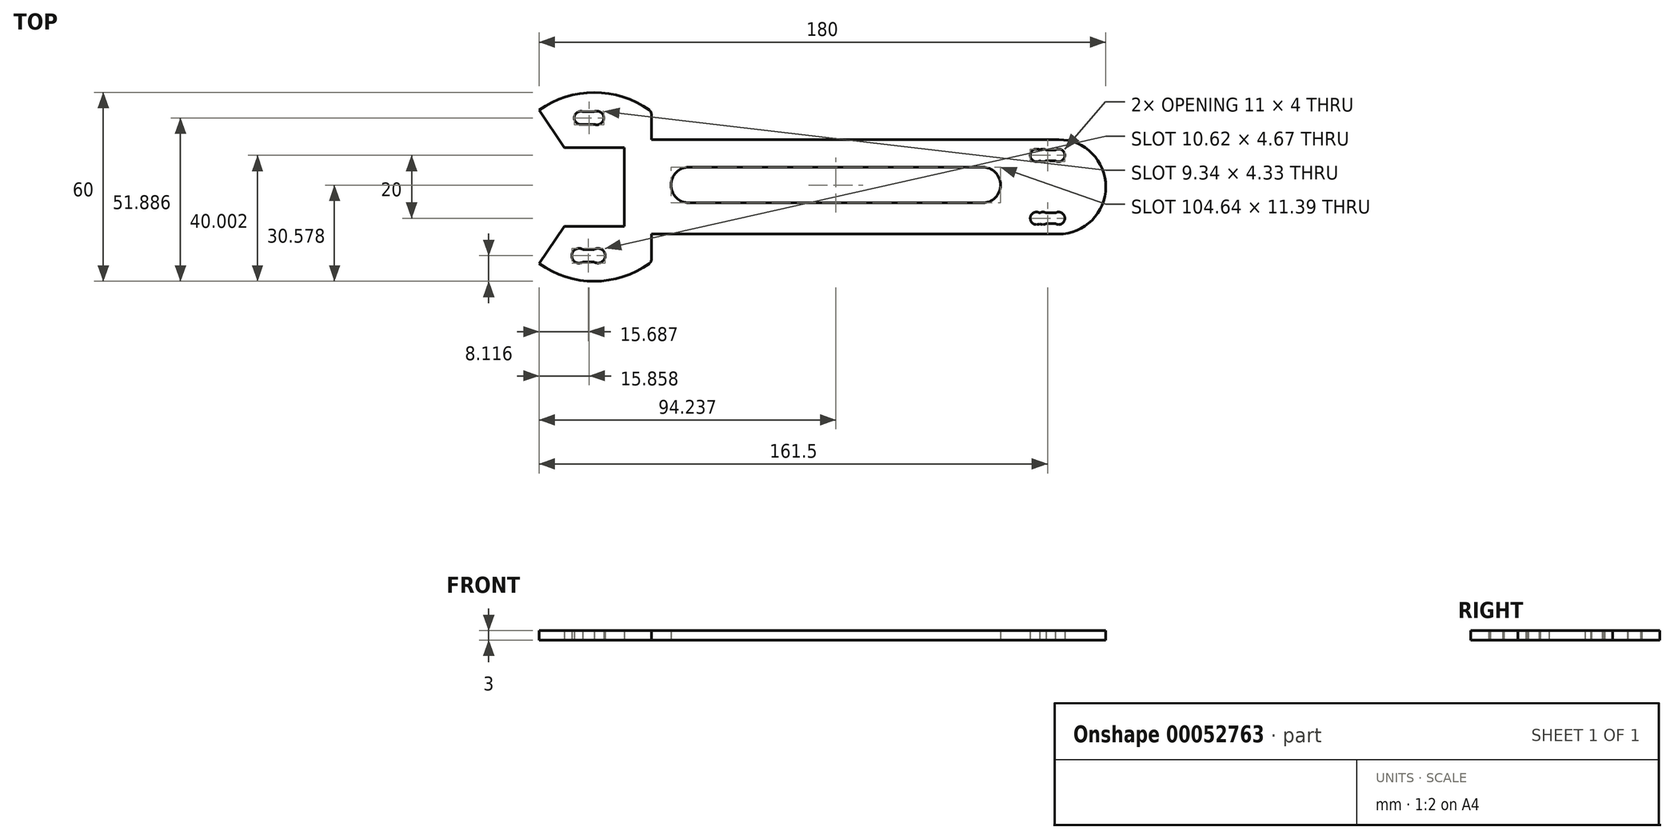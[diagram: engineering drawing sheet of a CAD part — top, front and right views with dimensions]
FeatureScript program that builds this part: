
annotation { "Feature Type Name" : "Feature", "Feature Type Description" : "" }
export const myFeature = defineFeature(function(context is Context, id is Id, definition is map)
    precondition{}
    {
        {
            var Q0;
            Q0=qCreatedBy(makeId("Top.planeOp"),FACE);
            var sketch = newSketch(context, id + "F0", { "sketchPlane" : qUnion([Q0])});
            skLineSegment(sketch, "E0.left", {"start": v(-8.16, -5.77) * mm, "end": v(-8.16, 19.23) * mm});
            skLineSegment(sketch, "E0.right", {"start": v(10.84, -5.77) * mm, "end": v(10.84, 19.23) * mm});
            skArc(sketch, "E1", {"start": v(-16.16, -17.64) * mm, "mid": v(1.75, -23.27) * mm, "end": v(19.5, -17.15) * mm});
            skPoint(sketch, "E2", {"position": v(10.84, 6.73) * mm});
            skLineSegment(sketch, "E3", {"start": v(10.84, 15.23) * mm, "end": v(-8.16, 19.23) * mm});
            skLineSegment(sketch, "E4", {"start": v(10.84, -1.77) * mm, "end": v(8.22, -2.32) * mm});
            skLineSegment(sketch, "E5", {"start": v(10.84, 15.23) * mm, "end": v(10.84, -1.77) * mm});
            skLineSegment(sketch, "E6", {"start": v(-8.16, -5.77) * mm, "end": v(10.84, -5.77) * mm});
            skLineSegment(sketch, "E7", {"start": v(10.84, 19.23) * mm, "end": v(-8.16, 19.23) * mm});
            skLineSegment(sketch, "E8", {"start": v(8.22, -2.32) * mm, "end": v(10.84, -5.77) * mm});
            skLineSegment(sketch, "E9.bottom", {"start": v(153.84, 30.62) * mm, "end": v(153.84, 30.62) * mm});
            skLineSegment(sketch, "E9.top", {"start": v(153.84, -17.15) * mm, "end": v(153.84, -17.15) * mm});
            skLineSegment(sketch, "E10", {"start": v(-16.16, 31.1) * mm, "end": v(-8.16, 19.23) * mm});
            skLineSegment(sketch, "E11", {"start": v(-8.16, -5.77) * mm, "end": v(-16.16, -17.64) * mm});
            skPoint(sketch, "E12", {"position": v(153.84, 6.73) * mm});
            skLineSegment(sketch, "E13", {"start": v(153.84, 6.73) * mm, "end": v(153.84, 6.73) * mm});
            skArc(sketch, "E14.trimOffspring", {"start": v(19.5, 30.62) * mm, "mid": v(1.75, 36.73) * mm, "end": v(-16.16, 31.1) * mm});
            skLineSegment(sketch, "E15.0", {"start": v(148.84, 16.73) * mm, "end": v(148.84, -3.27) * mm, "construction": true});
            skPoint(sketch, "E16", {"position": v(148.84, 6.73) * mm});
            skPoint(sketch, "E17", {"position": v(148.84, 16.73) * mm});
            skPoint(sketch, "E18", {"position": v(148.84, -3.27) * mm});
            skPoint(sketch, "E19.orphan", {"position": v(148.84, 30.62) * mm});
            skPoint(sketch, "E20.orphan", {"position": v(148.84, -17.15) * mm});
            skArc(sketch, "E21", {"start": v(147.84, 15) * mm, "mid": v(150.84, 16.73) * mm, "end": v(147.84, 18.46) * mm});
            skArc(sketch, "E22", {"start": v(147.84, -5) * mm, "mid": v(150.84, -3.27) * mm, "end": v(147.84, -1.54) * mm});
            skArc(sketch, "E23", {"start": v(148.84, -8.27) * mm, "mid": v(163.84, 6.77) * mm, "end": v(148.78, 21.73) * mm});
            skLineSegment(sketch, "E24", {"start": v(148.84, -8.27) * mm, "end": v(19.5, -8.27) * mm});
            skLineSegment(sketch, "E25", {"start": v(148.9, 21.73) * mm, "end": v(19.5, 21.73) * mm});
            skLineSegment(sketch, "E26", {"start": v(19.5, 21.73) * mm, "end": v(19.5, 30.62) * mm});
            skLineSegment(sketch, "E27", {"start": v(19.5, -8.27) * mm, "end": v(19.5, -17.15) * mm});
            skPoint(sketch, "E28.0.start.orphan", {"position": v(153.84, 30.62) * mm});
            skPoint(sketch, "E29.orphan", {"position": v(-8.16, 6.73) * mm});
            skLineSegment(sketch, "E30", {"start": v(1.34, 6.73) * mm, "end": v(1.34, 30.62) * mm});
            skLineSegment(sketch, "E31", {"start": v(1.34, 30.62) * mm, "end": v(1.34, -17.15) * mm});
            skLineSegment(sketch, "E32.bottom", {"start": v(1.34, 30.62) * mm, "end": v(-2.25, 30.62) * mm});
            skLineSegment(sketch, "E32.top", {"start": v(1.34, 26.62) * mm, "end": v(-2.25, 26.62) * mm});
            skLineSegment(sketch, "E32.left", {"start": v(1.34, 30.62) * mm, "end": v(1.34, 26.62) * mm});
            skLineSegment(sketch, "E32.right", {"start": v(-2.25, 30.62) * mm, "end": v(-2.25, 26.62) * mm});
            skLineSegment(sketch, "E33.bottom", {"start": v(1.34, -17.15) * mm, "end": v(-2.25, -17.15) * mm});
            skLineSegment(sketch, "E33.top", {"start": v(1.34, -13.15) * mm, "end": v(-2.25, -13.15) * mm});
            skLineSegment(sketch, "E33.left", {"start": v(1.34, -17.15) * mm, "end": v(1.34, -13.15) * mm});
            skLineSegment(sketch, "E33.right", {"start": v(-2.25, -17.15) * mm, "end": v(-2.25, -13.15) * mm});
            skCircle(sketch, "E34", {"center": v(-2.88, 28.62) * mm, "radius": 2.1 * mm});
            skPoint(sketch, "E34.third.point", {"position": v(-4.97, 28.62) * mm});
            skPoint(sketch, "E34.third.point.positionSnap0", {"position": v(-2.25, 28.62) * mm});
            skCircle(sketch, "E35", {"center": v(2.2, 28.62) * mm, "radius": 2.18 * mm});
            skPoint(sketch, "E35.third.point", {"position": v(3.05, 26.62) * mm});
            skCircle(sketch, "E36", {"center": v(-3.45, -15.15) * mm, "radius": 2.33 * mm});
            skPoint(sketch, "E36.third.point", {"position": v(-4.65, -17.15) * mm});
            skCircle(sketch, "E37", {"center": v(2.52, -15.15) * mm, "radius": 2.32 * mm});
            skPoint(sketch, "E37.third.point", {"position": v(3.7, -17.15) * mm});
            skLineSegment(sketch, "E38.bottom", {"start": v(31.46, 13) * mm, "end": v(124.7, 13) * mm});
            skLineSegment(sketch, "E38.top", {"start": v(31.46, 1.61) * mm, "end": v(124.7, 1.61) * mm});
            skLineSegment(sketch, "E38.left", {"start": v(31.46, 13) * mm, "end": v(31.46, 1.61) * mm});
            skLineSegment(sketch, "E38.right", {"start": v(124.7, 13) * mm, "end": v(124.7, 1.61) * mm});
            skArc(sketch, "E39", {"start": v(31.46, 13) * mm, "mid": v(25.76, 7.3) * mm, "end": v(31.46, 1.61) * mm});
            skArc(sketch, "E40", {"start": v(124.7, 1.61) * mm, "mid": v(130.4, 7.3) * mm, "end": v(124.7, 13) * mm});
            skLineSegment(sketch, "E41.0", {"start": v(141.84, 16.73) * mm, "end": v(141.84, -3.27) * mm, "construction": true});
            skLineSegment(sketch, "E42.0", {"start": v(143.84, 16.73) * mm, "end": v(143.84, -3.27) * mm, "construction": true});
            skArc(sketch, "E43", {"start": v(142.84, 15) * mm, "mid": v(143.84, 14.73) * mm, "end": v(144.84, 15) * mm});
            skArc(sketch, "E44", {"start": v(142.84, -1.54) * mm, "mid": v(139.84, -3.27) * mm, "end": v(142.84, -5) * mm});
            skArc(sketch, "E45", {"start": v(142.84, 18.46) * mm, "mid": v(139.84, 16.73) * mm, "end": v(142.84, 15) * mm});
            skArc(sketch, "E46", {"start": v(142.84, -5) * mm, "mid": v(143.84, -5.27) * mm, "end": v(144.84, -5) * mm});
            skLineSegment(sketch, "E47", {"start": v(144.84, 18.46) * mm, "end": v(147.84, 18.46) * mm, "construction": true});
            skLineSegment(sketch, "E48", {"start": v(144.84, -5) * mm, "end": v(147.84, -5) * mm});
            skLineSegment(sketch, "E49", {"start": v(144.84, 18.46) * mm, "end": v(147.84, 18.46) * mm});
            skLineSegment(sketch, "E50", {"start": v(142.84, 15) * mm, "end": v(143.84, 15) * mm});
            skArc(sketch, "E51.trimOffspring", {"start": v(144.84, 18.46) * mm, "mid": v(143.84, 18.73) * mm, "end": v(142.84, 18.46) * mm});
            skLineSegment(sketch, "E52.trimOffspring", {"start": v(144.84, 15) * mm, "end": v(147.84, 15) * mm});
            skLineSegment(sketch, "E53.trimOffspring", {"start": v(144.84, -1.54) * mm, "end": v(147.84, -1.54) * mm});
            skArc(sketch, "E54.trimOffspring", {"start": v(144.84, -1.54) * mm, "mid": v(143.84, -1.27) * mm, "end": v(142.84, -1.54) * mm});
            skSolve(sketch);
        }
        {
            var Q0;
            Q0=makeQuery(id+"F0.imprint","IMPRINT",FACE,{"disambiguationData":[TD([[makeQuery(id+"F0.imprint","IMPRINT",EDGE,{"derivedFrom":sQuery(id+"F0.wireOp",EDGE,"E1")}),1.0]])]});
            extrude(context, id + "F1", {"entities" : qUnion([Q0]), "depth" : 3 * mm});
        }
        {
            var Q0;
            Q0=makeQuery(id+"F1.opExtrude","SWEPT_EDGE",EDGE,{"disambiguationData":[OSD([sQuery(id+"F0.wireOp",EDGE,"E1"),sQuery(id+"F0.wireOp",EDGE,"E27")])]});
            var Q1;
            Q1=makeQuery(id+"F1.opExtrude","SWEPT_EDGE",EDGE,{"disambiguationData":[OSD([sQuery(id+"F0.wireOp",EDGE,"E14.trimOffspring"),sQuery(id+"F0.wireOp",EDGE,"E26")])]});
            fillet(context, id + "F2", {"entities" : qUnion([Q0, Q1]), "radius" : 1.5 * mm, "tangentPropagation" : true, "allowEdgeOverflow" : false});
        }
    });
